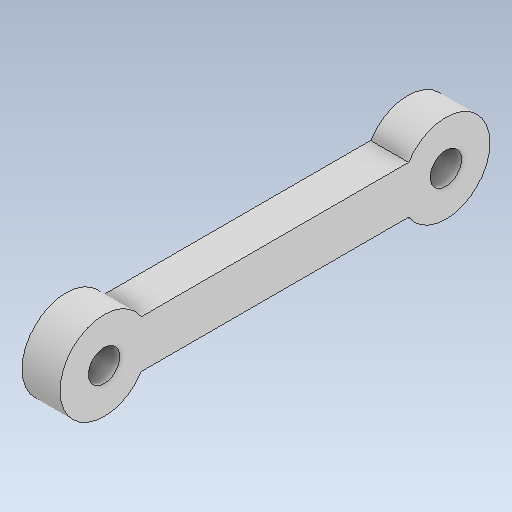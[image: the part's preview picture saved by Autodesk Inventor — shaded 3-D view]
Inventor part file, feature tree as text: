
AUTODESK INVENTOR PART (.ipt)
format: ipt  version: 2020 (Build 240168000, 168)  size: 117,760 bytes
history: native  units: in
note: dims shown in document units (in); Inventor stores cm internally (conversion verified against a paired STEP export)
features: extrude x1, sketch x1
ambient origin geometry x8: Origin, YZ Plane, XZ Plane, XY Plane, X Axis, Y Axis, Z Axis, Center Point
bodies: Solid1 (feature_tree)
feature tree (2):
  extrude  "Extrusion1"  Depth=1.4173in
  sketch  "Sketch1"  dims[d0=0.1299in d1=1.4173in d2=0.1181in d3=0.1181in d4=0.1969in d5=0.1575in d6=0.0in]
